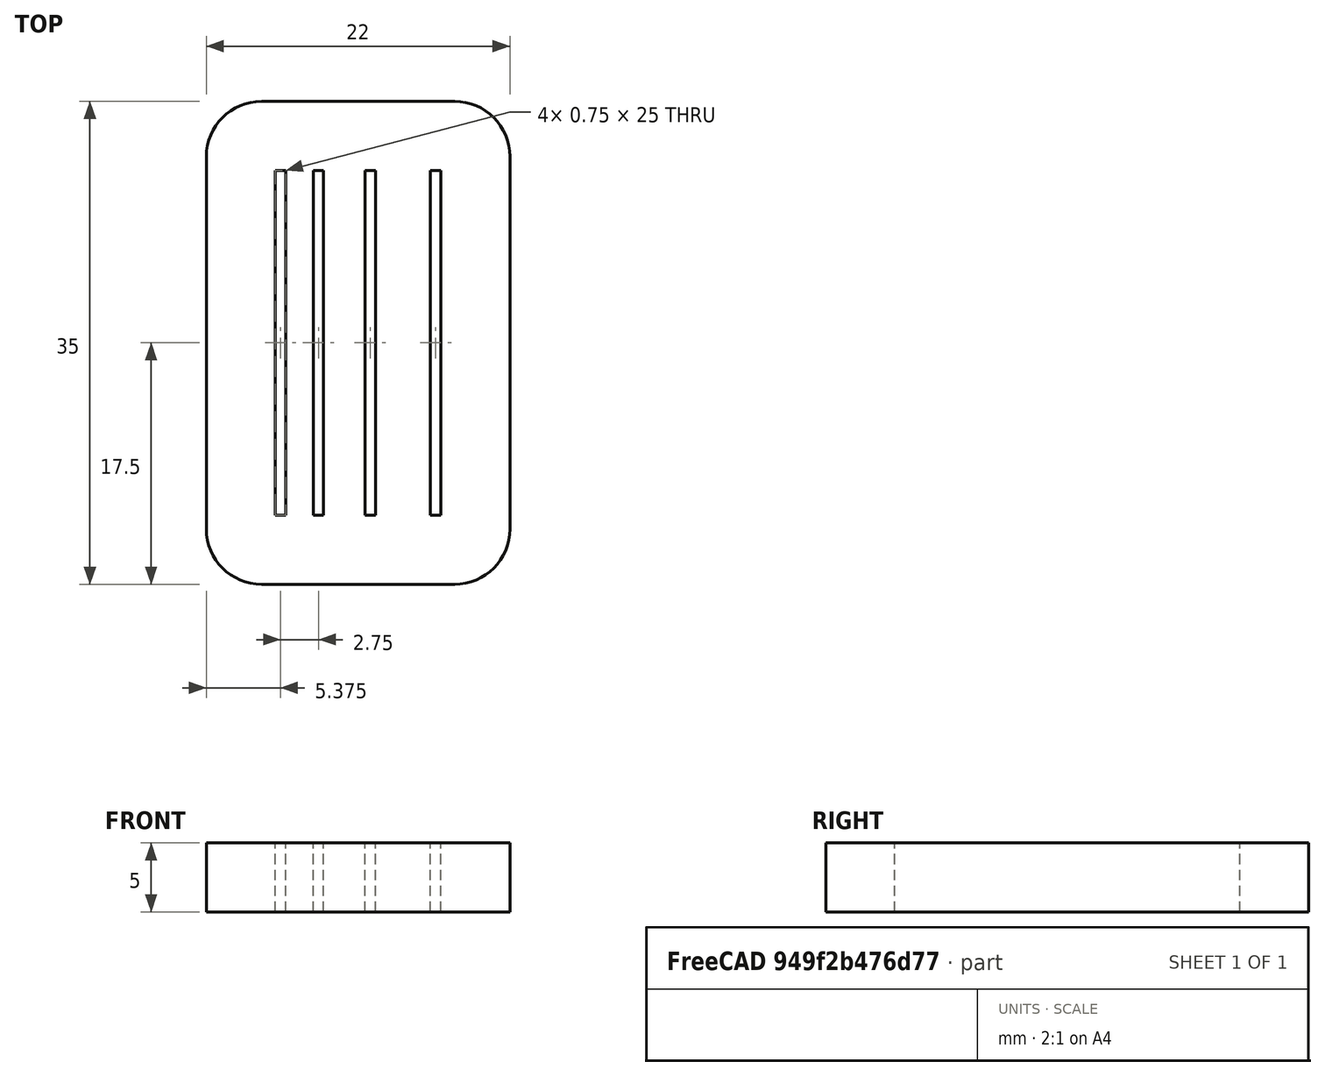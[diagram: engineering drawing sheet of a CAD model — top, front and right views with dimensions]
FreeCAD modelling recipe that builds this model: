
FCSTD DOCUMENT  (FreeCAD 0.19R24276 (Git))
Label: KuttingGuide
License: All rights reserved
LicenseURL: http://en.wikipedia.org/wiki/All_rights_reserved
objects: Part::Box×5, Part::MultiFuse×1, Part::Fillet×1, Part::Cut×1
note: 8 computed .brp shape members not serialized (recipe doc carries the construction recipe); baked Part::Feature solids carry a one-line shape summary decoded from their .brp

FEATURE [Part::Box] Box  label="Cube"
  AttacherType = Attacher::AttachEngine3D
  Height = 5
  Length = 22
  Width = 35
FEATURE [Part::Box] Box001  label="Cube001"
  AttacherType = Attacher::AttachEngine3D
  Height = 10
  Length = 0.75
  Placement = pos=(5,5,0) rot=(0,0,1;0rad)
  Width = 25
FEATURE [Part::Box] Box002  label="Cube002"
  AttacherType = Attacher::AttachEngine3D
  Height = 10
  Length = 0.75
  Placement = pos=(11.5,5,0) rot=(0,0,1;0rad)
  Width = 25
FEATURE [Part::Box] Box003  label="Cube003"
  AttacherType = Attacher::AttachEngine3D
  Height = 10
  Length = 0.75
  Placement = pos=(7.75,5,0) rot=(0,0,1;0rad)
  Width = 25
FEATURE [Part::Box] Box004  label="Cube004"
  AttacherType = Attacher::AttachEngine3D
  Height = 10
  Length = 0.75
  Placement = pos=(16.25,5,0) rot=(0,0,1;0rad)
  Width = 25
FEATURE [Part::MultiFuse] Fusion
  Shapes = -> [Box001,Box002,Box003,Box004]
FEATURE [Part::Fillet] Fillet
  Base = -> Box
  Edges = 4 edges r=4: [Edge1,Edge3,Edge5,Edge7]
FEATURE [Part::Cut] Cut
  Base = -> Fillet
  Tool = -> Fusion
